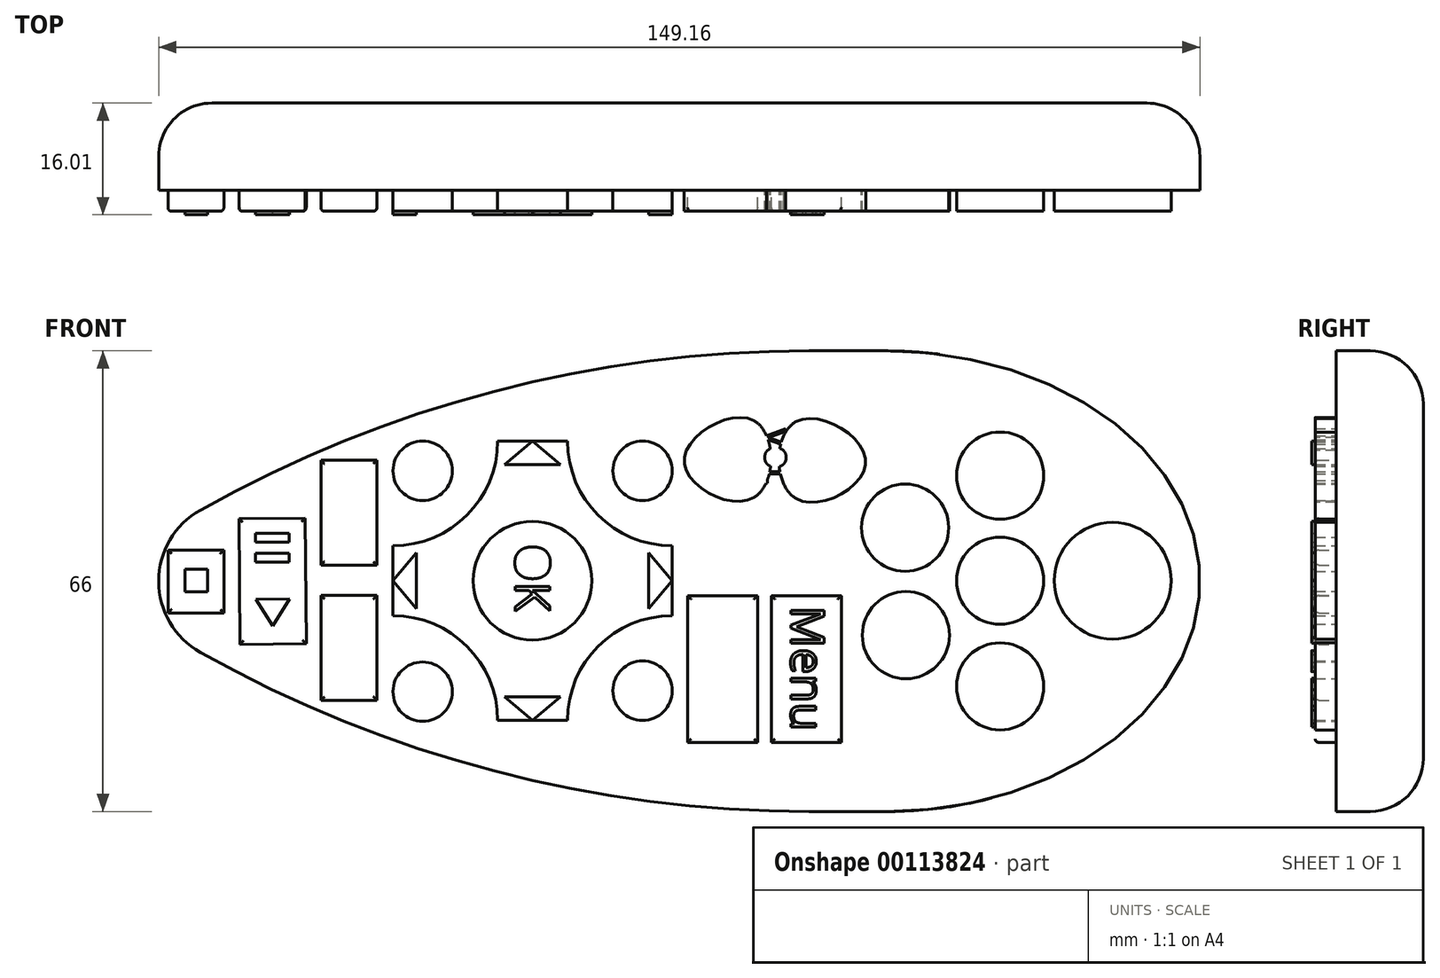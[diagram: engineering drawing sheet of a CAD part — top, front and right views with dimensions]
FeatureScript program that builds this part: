
annotation { "Feature Type Name" : "Feature", "Feature Type Description" : "" }
export const myFeature = defineFeature(function(context is Context, id is Id, definition is map)
    precondition{}
    {
        {
            var Q0;
            Q0=qCreatedBy(makeId("Front.planeOp"),FACE);
            var sketch = newSketch(context, id + "F0", { "sketchPlane" : qUnion([Q0])});
            skLineSegment(sketch, "E0.bottom", {"start": v(19.6, 32.93) * mm, "end": v(30.6, 32.93) * mm});
            skLineSegment(sketch, "E0.top", {"start": v(19.6, -33.07) * mm, "end": v(30.6, -33.07) * mm});
            skPoint(sketch, "E1", {"position": v(30.6, 32.93) * mm});
            skPoint(sketch, "E2", {"position": v(30.6, -33.07) * mm});
            skEllipticalArc(sketch, "E3", {});
            skPoint(sketch, "E4", {"position": v(19.6, 32.93) * mm});
            skPoint(sketch, "E5", {"position": v(19.6, -33.07) * mm});
            skArc(sketch, "E6", {"start": v(19.6, 32.93) * mm, "mid": v(-25.47, 27.13) * mm, "end": v(-67.6, 10.12) * mm});
            skArc(sketch, "E7", {"start": v(-67.6, -10.26) * mm, "mid": v(-25.47, -27.27) * mm, "end": v(19.6, -33.07) * mm});
            skArc(sketch, "E8", {"start": v(-67.6, 10.12) * mm, "mid": v(-71.85, 6.01) * mm, "end": v(-73.56, 0.35) * mm});
            skArc(sketch, "E9.trimOffspring", {"start": v(-73.56, 0.35) * mm, "mid": v(-72.07, -5.79) * mm, "end": v(-67.6, -10.26) * mm});
            skLineSegment(sketch, "E10.bottom", {"start": v(80, -33.5) * mm, "end": v(-80, -33.5) * mm});
            skLineSegment(sketch, "E10.top", {"start": v(80, 33.5) * mm, "end": v(-80, 33.5) * mm});
            skLineSegment(sketch, "E10.left", {"start": v(80, -33.5) * mm, "end": v(80, 33.5) * mm});
            skLineSegment(sketch, "E10.right", {"start": v(-80, -33.5) * mm, "end": v(-80, 33.5) * mm});
            skPoint(sketch, "E10.middle", {"position": v(0, 0) * mm});
            const initialGuessF0  = {"E3": [0.030595210015773783, -6.966936082444461e-05, 1, 0, 0.045, 0.033000011489756925, 4.71238898038469, 1.5707963267948966]};
            skSetInitialGuess(sketch, initialGuessF0);
            skSolve(sketch);
        }
        {
            var Q0;
            {var subQ0=sQuery(id+"F0.wireOp",EDGE,"E0.bottom");Q0=makeQuery(id+"F0.imprint","IMPRINT",FACE,{"disambiguationData":[TD([[makeQuery(id+"F0.imprint","IMPRINT",EDGE,{"derivedFrom":subQ0}),-1.0]])]});}
            var Q1;
            {var subQ0=sQuery(id+"F0.wireOp",EDGE,"E0.top");Q1=makeQuery(id+"F0.imprint","IMPRINT",FACE,{"disambiguationData":[TD([[makeQuery(id+"F0.imprint","IMPRINT",EDGE,{"derivedFrom":subQ0}),1.0]])]});}
            extrude(context, id + "F1", {"entities" : qUnion([Q0, Q1]), "depth" : 12.5 * mm});
        }
        {
            var Q0;
            Q0=makeQuery(id+"F1.opExtrude","CAP_FACE",FACE,{"disambiguationData":[OSD([sQuery(id+"F0.wireOp",EDGE,"E0.bottom"),sQuery(id+"F0.wireOp",EDGE,"E0.top"),sQuery(id+"F0.wireOp",EDGE,"E3"),sQuery(id+"F0.wireOp",EDGE,"E6"),sQuery(id+"F0.wireOp",EDGE,"E7"),sQuery(id+"F0.wireOp",EDGE,"E8"),sQuery(id+"F0.wireOp",EDGE,"E9.trimOffspring")])],"isStart":true});
            fillet(context, id + "F2", {"entities" : qUnion([Q0]), "radius" : 7.62 * mm, "tangentPropagation" : true, "allowEdgeOverflow" : false});
        }
        {
            var Q0;
            Q0=makeQuery(id+"F1.opExtrude","CAP_FACE",FACE,{"disambiguationData":[OSD([sQuery(id+"F0.wireOp",EDGE,"E0.bottom"),sQuery(id+"F0.wireOp",EDGE,"E0.top"),sQuery(id+"F0.wireOp",EDGE,"E3"),sQuery(id+"F0.wireOp",EDGE,"E6"),sQuery(id+"F0.wireOp",EDGE,"E7"),sQuery(id+"F0.wireOp",EDGE,"E8"),sQuery(id+"F0.wireOp",EDGE,"E9.trimOffspring")])],"isStart":false});
            var sketch = newSketch(context, id + "F3", { "sketchPlane" : qUnion([Q0])});
            skCircle(sketch, "E11", {"center": v(63.1, 0) * mm, "radius": 8.37 * mm});
            skCircle(sketch, "E12", {"center": v(46.98, 0) * mm, "radius": 6.25 * mm});
            skCircle(sketch, "E13", {"center": v(46.98, 15.06) * mm, "radius": 6.25 * mm});
            skCircle(sketch, "E14", {"center": v(46.98, -15.14) * mm, "radius": 6.25 * mm});
            skCircle(sketch, "E15", {"center": v(33.37, 7.6) * mm, "radius": 6.25 * mm});
            skCircle(sketch, "E16", {"center": v(33.48, -7.8) * mm, "radius": 6.25 * mm});
            skLineSegment(sketch, "E17", {"start": v(17.72, 11.79) * mm, "end": v(17.72, 22.79) * mm});
            skFitSpline(sketch, "E18", {"points": [v(17.72, 22.79) * mm, v(27.72, 17) * mm, v(17.72, 11.79) * mm, v(17.72, 22.79) * mm]});
            skLineSegment(sketch, "E19", {"start": v(11.72, 22.93) * mm, "end": v(11.72, 11.93) * mm});
            skFitSpline(sketch, "E20", {"points": [v(11.72, 11.93) * mm, v(1.72, 17.15) * mm, v(11.72, 22.93) * mm, v(11.72, 11.93) * mm]});
            skText(sketch, "E21", { "text": "VOL", "fontName": "OpenSans-Regular.ttf"});
            skLineSegment(sketch, "E22.bottom", {"start": v(24.22, -2.16) * mm, "end": v(14.22, -2.16) * mm});
            skLineSegment(sketch, "E22.top", {"start": v(24.22, -23.16) * mm, "end": v(14.22, -23.16) * mm});
            skLineSegment(sketch, "E22.left", {"start": v(24.22, -2.16) * mm, "end": v(24.22, -23.16) * mm});
            skLineSegment(sketch, "E22.right", {"start": v(14.22, -2.16) * mm, "end": v(14.22, -23.16) * mm});
            skLineSegment(sketch, "E23.bottom", {"start": v(12.22, -2.16) * mm, "end": v(2.22, -2.16) * mm});
            skLineSegment(sketch, "E23.top", {"start": v(12.22, -23.16) * mm, "end": v(2.22, -23.16) * mm});
            skLineSegment(sketch, "E23.left", {"start": v(12.22, -2.16) * mm, "end": v(12.22, -23.16) * mm});
            skLineSegment(sketch, "E23.right", {"start": v(2.22, -2.16) * mm, "end": v(2.22, -23.16) * mm});
            skArc(sketch, "E24", {"start": v(0, -5) * mm, "mid": v(-10.6, -9.4) * mm, "end": v(-15, -20) * mm});
            skPoint(sketch, "E25", {"position": v(-15, -20) * mm});
            skPoint(sketch, "E26", {"position": v(0, -5) * mm});
            skArc(sketch, "E27", {"start": v(-15, 20) * mm, "mid": v(-10.6, 9.4) * mm, "end": v(0, 5) * mm});
            skPoint(sketch, "E28", {"position": v(-15, 20) * mm});
            skPoint(sketch, "E29", {"position": v(0, 5) * mm});
            skLineSegment(sketch, "E30", {"start": v(0, 5) * mm, "end": v(0, -5) * mm});
            skPoint(sketch, "E31", {"position": v(-25, 20) * mm});
            skArc(sketch, "E32", {"start": v(-40, 5) * mm, "mid": v(-29.4, 9.4) * mm, "end": v(-25, 20) * mm});
            skLineSegment(sketch, "E33", {"start": v(0, 0) * mm, "end": v(-191.16, 0) * mm});
            skArc(sketch, "E34", {"start": v(-25, -20) * mm, "mid": v(-29.4, -9.4) * mm, "end": v(-40, -5) * mm});
            skPoint(sketch, "E35", {"position": v(-25, -20) * mm});
            skPoint(sketch, "E36", {"position": v(-40, 0) * mm});
            skPoint(sketch, "E36.positionSnap0", {"position": v(-40, 5) * mm});
            skPoint(sketch, "E37", {"position": v(-40, -5) * mm});
            skLineSegment(sketch, "E38", {"start": v(-25, 20) * mm, "end": v(-15, 20) * mm});
            skLineSegment(sketch, "E39", {"start": v(-40, 5) * mm, "end": v(-40, -5) * mm});
            skLineSegment(sketch, "E40", {"start": v(-25, -20) * mm, "end": v(-15, -20) * mm});
            skLineSegment(sketch, "E41", {"start": v(0, -5) * mm, "end": v(0, 5) * mm});
            skPoint(sketch, "E42.start.orphan", {"position": v(-20, 20) * mm});
            skCircle(sketch, "E43", {"center": v(-35.75, 15.75) * mm, "radius": 4.25 * mm});
            skCircle(sketch, "E44", {"center": v(-35.75, -15.9) * mm, "radius": 4.25 * mm});
            skCircle(sketch, "E45", {"center": v(-4.25, -15.75) * mm, "radius": 4.25 * mm});
            skCircle(sketch, "E46", {"center": v(-4.25, 15.75) * mm, "radius": 4.25 * mm});
            skLineSegment(sketch, "E47.trimOffspring", {"start": v(-15, -20) * mm, "end": v(-25, -20) * mm});
            skLineSegment(sketch, "E48.trimOffspring", {"start": v(-40, -5) * mm, "end": v(-40, 5) * mm});
            skLineSegment(sketch, "E49.bottom", {"start": v(-61.93, -9.11) * mm, "end": v(-52.43, -9.03) * mm});
            skLineSegment(sketch, "E49.top", {"start": v(-62.07, 8.89) * mm, "end": v(-52.57, 8.97) * mm});
            skLineSegment(sketch, "E49.left", {"start": v(-61.93, -9.11) * mm, "end": v(-62.07, 8.89) * mm});
            skLineSegment(sketch, "E49.right", {"start": v(-52.43, -9.03) * mm, "end": v(-52.57, 8.97) * mm});
            skLineSegment(sketch, "E50.bottom", {"start": v(-42.3, -2.12) * mm, "end": v(-50.3, -2.12) * mm});
            skLineSegment(sketch, "E50.top", {"start": v(-42.3, -17.12) * mm, "end": v(-50.3, -17.12) * mm});
            skLineSegment(sketch, "E50.left", {"start": v(-42.3, -2.12) * mm, "end": v(-42.3, -17.12) * mm});
            skLineSegment(sketch, "E50.right", {"start": v(-50.3, -2.12) * mm, "end": v(-50.3, -17.12) * mm});
            skLineSegment(sketch, "E51.bottom", {"start": v(-42.33, 17.24) * mm, "end": v(-50.33, 17.24) * mm});
            skLineSegment(sketch, "E51.top", {"start": v(-42.33, 2.24) * mm, "end": v(-50.33, 2.24) * mm});
            skLineSegment(sketch, "E51.left", {"start": v(-42.33, 17.24) * mm, "end": v(-42.33, 2.24) * mm});
            skLineSegment(sketch, "E51.right", {"start": v(-50.33, 17.24) * mm, "end": v(-50.33, 2.24) * mm});
            skLineSegment(sketch, "E52.bottom", {"start": v(-72.23, 4.39) * mm, "end": v(-64.23, 4.39) * mm});
            skLineSegment(sketch, "E52.top", {"start": v(-72.23, -4.61) * mm, "end": v(-64.23, -4.61) * mm});
            skLineSegment(sketch, "E52.left", {"start": v(-72.23, 4.39) * mm, "end": v(-72.23, -4.61) * mm});
            skLineSegment(sketch, "E52.right", {"start": v(-64.23, 4.39) * mm, "end": v(-64.23, -4.61) * mm});
            const initialGuessF3  = {"E21": [0.0133, 0.02177, 0, -1, 0.003]};
            skSetInitialGuess(sketch, initialGuessF3);
            skSolve(sketch);
        }
        {
            var Q0;
            Q0 = qSketchRegion(id + "F3", true);
            extrude(context, id + "F4", {"entities" : qUnion([Q0]), "operationType" : NewBodyOperationType.ADD, "depth" : 3 * mm});
        }
        {
            var Q0;
            Q0=makeQuery(id+"F4.opExtrude","CAP_FACE",FACE,{"disambiguationData":[OSD([sQuery(id+"F3.wireOp",EDGE,"E23.bottom"),sQuery(id+"F3.wireOp",EDGE,"E23.top"),sQuery(id+"F3.wireOp",EDGE,"E23.left"),sQuery(id+"F3.wireOp",EDGE,"E23.right")])],"isStart":false});
            var Q1;
            Q1=makeQuery(id+"F4.opExtrude","CAP_FACE",FACE,{"disambiguationData":[OSD([sQuery(id+"F3.wireOp",EDGE,"E22.bottom"),sQuery(id+"F3.wireOp",EDGE,"E22.top"),sQuery(id+"F3.wireOp",EDGE,"E22.left"),sQuery(id+"F3.wireOp",EDGE,"E22.right")])],"isStart":false});
            var Q2;
            Q2=makeQuery(id+"F4.opExtrude","CAP_FACE",FACE,{"disambiguationData":[OSD([sQuery(id+"F3.wireOp",EDGE,"E50.bottom"),sQuery(id+"F3.wireOp",EDGE,"E50.top"),sQuery(id+"F3.wireOp",EDGE,"E50.left"),sQuery(id+"F3.wireOp",EDGE,"E50.right")])],"isStart":false});
            var Q3;
            Q3=makeQuery(id+"F4.opExtrude","CAP_FACE",FACE,{"disambiguationData":[OSD([sQuery(id+"F3.wireOp",EDGE,"E49.bottom"),sQuery(id+"F3.wireOp",EDGE,"E49.top"),sQuery(id+"F3.wireOp",EDGE,"E49.left"),sQuery(id+"F3.wireOp",EDGE,"E49.right")])],"isStart":false});
            var Q4;
            Q4=makeQuery(id+"F4.opExtrude","CAP_FACE",FACE,{"disambiguationData":[OSD([sQuery(id+"F3.wireOp",EDGE,"E51.bottom"),sQuery(id+"F3.wireOp",EDGE,"E51.top"),sQuery(id+"F3.wireOp",EDGE,"E51.left"),sQuery(id+"F3.wireOp",EDGE,"E51.right")])],"isStart":false});
            var Q5;
            Q5=makeQuery(id+"F4.opExtrude","CAP_FACE",FACE,{"disambiguationData":[OSD([sQuery(id+"F3.wireOp",EDGE,"2VEgrcu2-VFI6-u6Ur-byTh-ITGL87VBiqVv.bottom"),sQuery(id+"F3.wireOp",EDGE,"2VEgrcu2-VFI6-u6Ur-byTh-ITGL87VBiqVv.top"),sQuery(id+"F3.wireOp",EDGE,"2VEgrcu2-VFI6-u6Ur-byTh-ITGL87VBiqVv.left"),sQuery(id+"F3.wireOp",EDGE,"2VEgrcu2-VFI6-u6Ur-byTh-ITGL87VBiqVv.right")])],"isStart":false});
            var Q6;
            Q6=makeQuery(id+"F4.opExtrude","CAP_FACE",FACE,{"disambiguationData":[OSD([sQuery(id+"F3.wireOp",EDGE,"E52.bottom"),sQuery(id+"F3.wireOp",EDGE,"E52.top"),sQuery(id+"F3.wireOp",EDGE,"E52.left"),sQuery(id+"F3.wireOp",EDGE,"E52.right")])],"isStart":false});
            fillet(context, id + "F5", {"entities" : qUnion([Q0, Q1, Q2, Q3, Q4, Q5, Q6]), "radius" : 0.5 * mm, "tangentPropagation" : true, "allowEdgeOverflow" : false});
        }
        {
            var Q0;
            Q0=makeQuery(id+"F4.opExtrude","CAP_FACE",FACE,{"disambiguationData":[OSD([sQuery(id+"F3.wireOp",EDGE,"E24"),sQuery(id+"F3.wireOp",EDGE,"E27"),sQuery(id+"F3.wireOp",EDGE,"E32"),sQuery(id+"F3.wireOp",EDGE,"E34"),sQuery(id+"F3.wireOp",EDGE,"E30"),sQuery(id+"F3.wireOp",EDGE,"E38"),sQuery(id+"F3.wireOp",EDGE,"E47.trimOffspring"),sQuery(id+"F3.wireOp",EDGE,"E48.trimOffspring")])],"isStart":false});
            var sketch = newSketch(context, id + "F6", { "sketchPlane" : qUnion([Q0])});
            skLineSegment(sketch, "E53.0", {"start": v(-57.2, -6.5) * mm, "end": v(-59.64, -2.65) * mm});
            skLineSegment(sketch, "E53.1", {"start": v(-59.64, -2.65) * mm, "end": v(-54.81, -2.62) * mm});
            skLineSegment(sketch, "E53.2", {"start": v(-54.81, -2.62) * mm, "end": v(-57.2, -6.5) * mm});
            skLineSegment(sketch, "E54.0", {"start": v(-36.64, -4) * mm, "end": v(-40, 0) * mm});
            skLineSegment(sketch, "E54.1", {"start": v(-40, 0) * mm, "end": v(-36.64, 4) * mm});
            skLineSegment(sketch, "E54.2", {"start": v(-36.64, 4) * mm, "end": v(-36.64, -4) * mm});
            skLineSegment(sketch, "E55.0", {"start": v(-24, 16.64) * mm, "end": v(-20, 20) * mm});
            skLineSegment(sketch, "E55.1", {"start": v(-20, 20) * mm, "end": v(-16, 16.64) * mm});
            skLineSegment(sketch, "E55.2", {"start": v(-16, 16.64) * mm, "end": v(-24, 16.64) * mm});
            skLineSegment(sketch, "E56.0", {"start": v(-16, -16.64) * mm, "end": v(-20, -20) * mm});
            skLineSegment(sketch, "E56.1", {"start": v(-20, -20) * mm, "end": v(-24, -16.64) * mm});
            skLineSegment(sketch, "E56.2", {"start": v(-24, -16.64) * mm, "end": v(-16, -16.64) * mm});
            skLineSegment(sketch, "E57.0", {"start": v(-3.36, 4) * mm, "end": v(0, 0) * mm});
            skLineSegment(sketch, "E57.1", {"start": v(0, 0) * mm, "end": v(-3.36, -4) * mm});
            skLineSegment(sketch, "E57.2", {"start": v(-3.36, -4) * mm, "end": v(-3.36, 4) * mm});
            skPoint(sketch, "E58.centerSnap0", {"position": v(-20, 4) * mm});
            skText(sketch, "E59", { "text": "OK", "fontName": "OpenSans-Regular.ttf"});
            skCircle(sketch, "E60", {"center": v(-20, 0) * mm, "radius": 8.5 * mm});
            skPoint(sketch, "E61.orphan", {"position": v(-16, 20) * mm});
            skPoint(sketch, "E62.trimOffspring.end.orphan", {"position": v(-24, 20) * mm});
            skPoint(sketch, "E63.trimOffspring.end.orphan", {"position": v(-16, -20) * mm});
            skPoint(sketch, "E64.start.orphan", {"position": v(-24, -20) * mm});
            skPoint(sketch, "E65.trimOffspring.end.orphan", {"position": v(0, -4) * mm});
            skPoint(sketch, "E66.trimOffspring.end.orphan", {"position": v(0, 4) * mm});
            skPoint(sketch, "E67", {"position": v(-42.83, 9.74) * mm});
            skPoint(sketch, "E68", {"position": v(-49.82, 9.74) * mm});
            skPoint(sketch, "E69", {"position": v(-42.8, -9.62) * mm});
            skPoint(sketch, "E70", {"position": v(-49.79, -9.62) * mm});
            skPoint(sketch, "E71", {"position": v(-53, -0.04) * mm});
            skPoint(sketch, "E72", {"position": v(-61.5, -0.1) * mm});
            skLineSegment(sketch, "E73", {"start": v(-42.83, 9.74) * mm, "end": v(-49.82, 9.74) * mm});
            skLineSegment(sketch, "E74", {"start": v(-49.79, -9.62) * mm, "end": v(-42.8, -9.62) * mm});
            skLineSegment(sketch, "E75", {"start": v(-61.5, -0.1) * mm, "end": v(-53, -0.04) * mm});
            skLineSegment(sketch, "E76.bottom", {"start": v(-69.8, 1.65) * mm, "end": v(-66.54, 1.65) * mm});
            skLineSegment(sketch, "E76.top", {"start": v(-69.8, -1.6) * mm, "end": v(-66.54, -1.6) * mm});
            skLineSegment(sketch, "E76.left", {"start": v(-69.8, 1.65) * mm, "end": v(-69.8, -1.6) * mm});
            skLineSegment(sketch, "E76.right", {"start": v(-66.54, 1.65) * mm, "end": v(-66.54, -1.6) * mm});
            skPoint(sketch, "E77", {"position": v(-57.32, 8.42) * mm});
            skPoint(sketch, "E78", {"position": v(-57.18, -8.56) * mm});
            skLineSegment(sketch, "E79", {"start": v(-57.32, 8.42) * mm, "end": v(-57.18, -8.56) * mm});
            skLineSegment(sketch, "E80.bottom", {"start": v(-54.86, 2.65) * mm, "end": v(-59.7, 2.65) * mm});
            skLineSegment(sketch, "E80.top", {"start": v(-54.86, 3.92) * mm, "end": v(-59.7, 3.92) * mm});
            skLineSegment(sketch, "E80.left", {"start": v(-54.86, 2.65) * mm, "end": v(-54.86, 3.92) * mm});
            skLineSegment(sketch, "E80.right", {"start": v(-59.7, 2.65) * mm, "end": v(-59.7, 3.92) * mm});
            skPoint(sketch, "E80.middle", {"position": v(-57.28, 3.29) * mm});
            skLineSegment(sketch, "E81", {"start": v(-59.68, 2.65) * mm, "end": v(-59.7, 3.92) * mm});
            skLineSegment(sketch, "E82.bottom", {"start": v(-54.89, 6.77) * mm, "end": v(-59.71, 6.77) * mm});
            skLineSegment(sketch, "E82.top", {"start": v(-54.89, 5.5) * mm, "end": v(-59.71, 5.5) * mm});
            skLineSegment(sketch, "E82.left", {"start": v(-54.89, 6.77) * mm, "end": v(-54.89, 5.5) * mm});
            skLineSegment(sketch, "E82.right", {"start": v(-59.71, 6.77) * mm, "end": v(-59.71, 5.5) * mm});
            skPoint(sketch, "E82.middle", {"position": v(-57.3, 6.13) * mm});
            skLineSegment(sketch, "E83.trimOffspring", {"start": v(-59.7, 5.5) * mm, "end": v(-59.71, 6.77) * mm});
            skLineSegment(sketch, "E84", {"start": v(22.04, 19.74) * mm, "end": v(22.04, 14.92) * mm});
            skLineSegment(sketch, "E85", {"start": v(19.82, 17.33) * mm, "end": v(24.26, 17.33) * mm});
            skLineSegment(sketch, "E86", {"start": v(6.88, 19.74) * mm, "end": v(6.88, 15.17) * mm});
            skText(sketch, "E87", { "text": "Menu", "fontName": "OpenSans-Regular.ttf"});
            const initialGuessF6  = {"E59": [-0.02248, 0.00527, 0, -1, 0.005], "E87": [0.01702, -0.00361, 0, -1, 0.0048]};
            skSetInitialGuess(sketch, initialGuessF6);
            skSolve(sketch);
        }
        {
            var Q0;
            Q0=sQuery(id+"F6.wireOp",EDGE,"E73");
            var Q1;
            Q1=sQuery(id+"F6.wireOp",EDGE,"E74");
            var Q2;
            Q2=sQuery(id+"F6.wireOp",EDGE,"E75");
            extrude(context, id + "F7", {"bodyType" : ToolBodyType.SURFACE, "surfaceEntities" : qUnion([Q0, Q1, Q2]), "endBound" : BoundingType.SYMMETRIC, "depth" : 0.03 * mm});
        }
        {
            var Q0;
            Q0=sQuery(id+"F6.wireOp",EDGE,"E86");
            var Q1;
            Q1=sQuery(id+"F6.wireOp",EDGE,"E85");
            extrude(context, id + "F8", {"bodyType" : ToolBodyType.SURFACE, "surfaceEntities" : qUnion([Q0, Q1]), "depth" : 0.5 * mm});
        }
        {
            var Q0;
            Q0=sQuery(id+"F6.wireOp",EDGE,"E84");
            extrude(context, id + "F9", {"bodyType" : ToolBodyType.SURFACE, "surfaceEntities" : qUnion([Q0]), "depth" : 0.5 * mm});
        }
        {
            var Q0;
            Q0 = qSketchRegion(id + "F6", true);
            extrude(context, id + "F10", {"entities" : qUnion([Q0]), "operationType" : NewBodyOperationType.ADD, "depth" : 0.5 * mm});
        }
        {
            var Q0;
            Q0=makeQuery(id+"F7.opExtrude","SWEPT_BODY",BODY,{"disambiguationData":[OSD([sQuery(id+"F6.wireOp",EDGE,"E74")])]});
            var Q1;
            Q1=makeQuery(id+"F7.opExtrude","SWEPT_BODY",BODY,{"disambiguationData":[OSD([sQuery(id+"F6.wireOp",EDGE,"E73")])]});
            deleteBodies(context, id + "F11", {"entities" : qUnion([Q0, Q1])});
        }
    });
